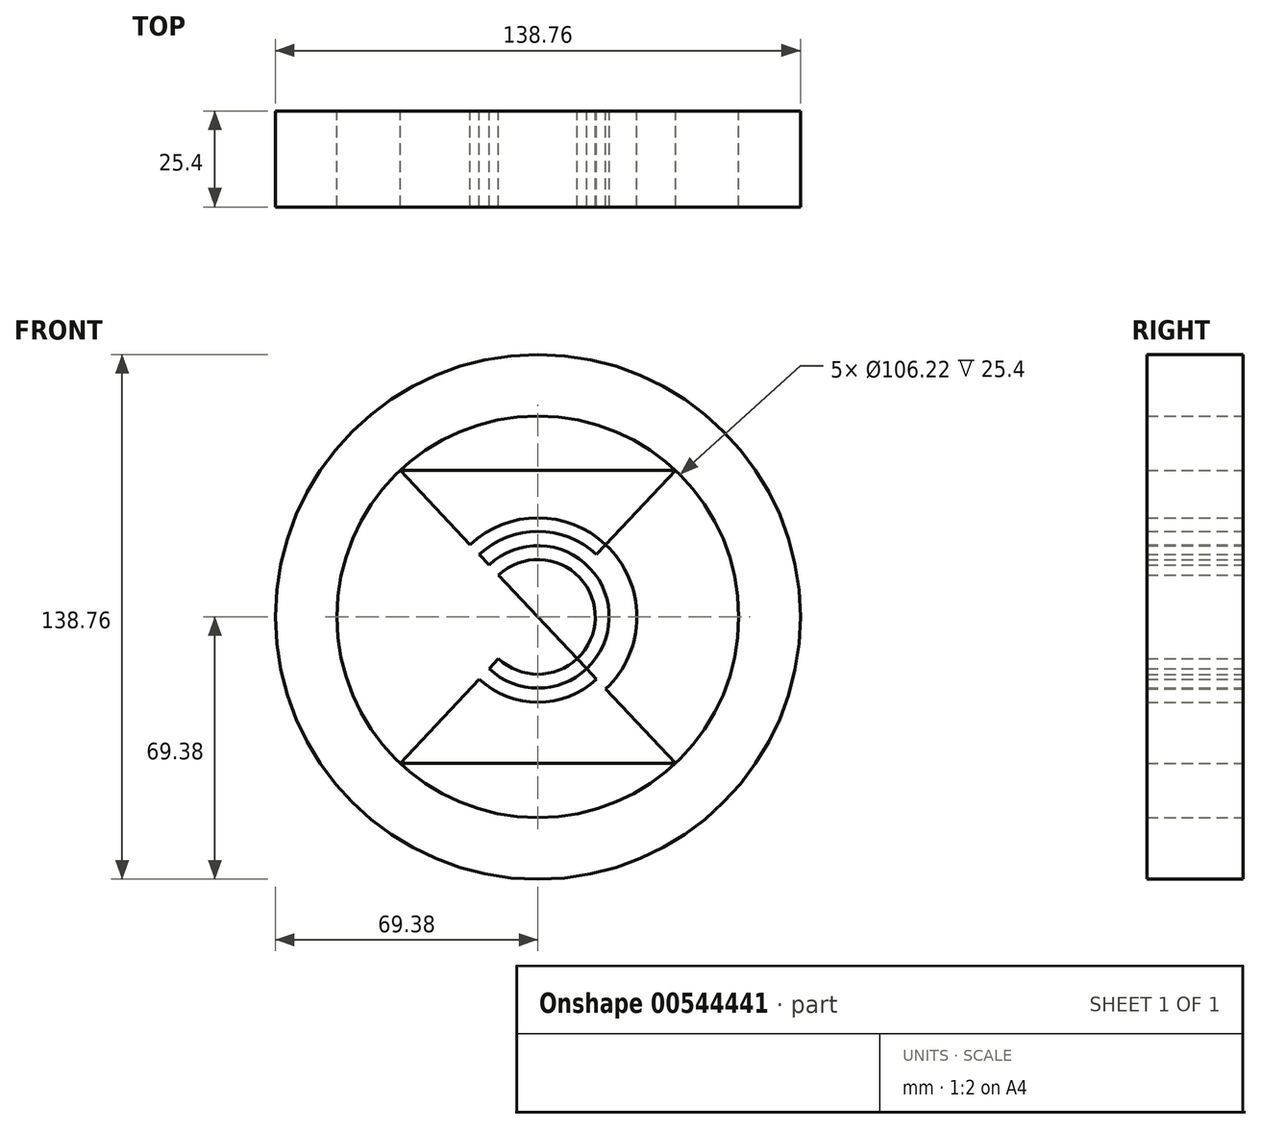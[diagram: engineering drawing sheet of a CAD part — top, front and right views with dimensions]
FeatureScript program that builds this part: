
annotation { "Feature Type Name" : "Feature", "Feature Type Description" : "" }
export const myFeature = defineFeature(function(context is Context, id is Id, definition is map)
    precondition{}
    {
        {
            var Q0;
            Q0=qCreatedBy(makeId("Front.planeOp"),FACE);
            var sketch = newSketch(context, id + "F0", { "sketchPlane" : qUnion([Q0])});
            skCircle(sketch, "E0", {"center": v(0, 0) * mm, "radius": 69.38 * mm});
            skCircle(sketch, "E1", {"center": v(0, 0) * mm, "radius": 63.29 * mm});
            skCircle(sketch, "E2", {"center": v(0, 0) * mm, "radius": 58 * mm});
            skCircle(sketch, "E3", {"center": v(0, 0) * mm, "radius": 53.11 * mm});
            skCircle(sketch, "E4", {"center": v(0, 0) * mm, "radius": 26.19 * mm});
            skCircle(sketch, "E5", {"center": v(0, 0) * mm, "radius": 22.6 * mm});
            skCircle(sketch, "E6", {"center": v(0, 0) * mm, "radius": 18.83 * mm});
            skCircle(sketch, "E7", {"center": v(0, 0) * mm, "radius": 15.17 * mm});
            skLineSegment(sketch, "E8", {"start": v(0, 0) * mm, "end": v(-36.38, 38.69) * mm});
            skLineSegment(sketch, "E9", {"start": v(-36.38, 38.69) * mm, "end": v(36.38, 38.69) * mm});
            skLineSegment(sketch, "E10", {"start": v(36.38, 38.69) * mm, "end": v(0, 0) * mm});
            skLineSegment(sketch, "E11", {"start": v(0, 0) * mm, "end": v(-36.38, -38.69) * mm});
            skLineSegment(sketch, "E12", {"start": v(-36.38, -38.69) * mm, "end": v(36.38, -38.69) * mm});
            skLineSegment(sketch, "E13", {"start": v(36.38, -38.69) * mm, "end": v(0, 0) * mm});
            skSolve(sketch);
        }
        {
            var Q0;
            Q0 = qSketchRegion(id + "F0", true);
            var Q1;
            {var subQ5=sQuery(id+"F0.wireOp",EDGE,"E12");Q1=makeQuery(id+"F0.imprint","IMPRINT",FACE,{"disambiguationData":[TD([[makeQuery(id+"F0.imprint","IMPRINT",EDGE,{"derivedFrom":subQ5}),1.0]])]});}
            var Q2;
            Q2=makeQuery(id+"F0.imprint","IMPRINT",FACE,{"disambiguationData":[TD([[makeQuery(id+"F0.imprint","IMPRINT",EDGE,{"derivedFrom":sQuery(id+"F0.wireOp",EDGE,"E2")}),1.0]])]});
            var Q3;
            {var subQ5=sQuery(id+"F0.wireOp",EDGE,"E9");Q3=makeQuery(id+"F0.imprint","IMPRINT",FACE,{"disambiguationData":[TD([[makeQuery(id+"F0.imprint","IMPRINT",EDGE,{"derivedFrom":subQ5}),-1.0]])]});}
            var Q4;
            {var subQ0=sQuery(id+"F0.wireOp",EDGE,"E8");var subQ1=sQuery(id+"F0.wireOp",EDGE,"E7");var subQ2=makeQuery(id+"F0.imprint","INTERSECT",VERTEX,{"derivedFrom":[subQ1,subQ0]});Q4=makeQuery(id+"F0.imprint","IMPRINT",FACE,{"disambiguationData":[TD([[makeQuery(id+"F0.imprint","IMPRINT",EDGE,{"disambiguationData":[TD([[subQ2,1.0]])],"derivedFrom":subQ1}),1.0]])]});}
            var Q5;
            {var subQ0=sQuery(id+"F0.wireOp",EDGE,"E11");var subQ1=sQuery(id+"F0.wireOp",EDGE,"E6");var subQ2=makeQuery(id+"F0.imprint","INTERSECT",VERTEX,{"derivedFrom":[subQ1,subQ0]});Q5=makeQuery(id+"F0.imprint","IMPRINT",FACE,{"disambiguationData":[TD([[makeQuery(id+"F0.imprint","IMPRINT",EDGE,{"disambiguationData":[TD([[subQ2,-1.0]])],"derivedFrom":subQ1}),1.0]])]});}
            var Q6;
            {var subQ0=sQuery(id+"F0.wireOp",EDGE,"E10");var subQ1=sQuery(id+"F0.wireOp",EDGE,"E5");var subQ2=makeQuery(id+"F0.imprint","INTERSECT",VERTEX,{"derivedFrom":[subQ1,subQ0]});Q6=makeQuery(id+"F0.imprint","IMPRINT",FACE,{"disambiguationData":[TD([[makeQuery(id+"F0.imprint","IMPRINT",EDGE,{"disambiguationData":[TD([[subQ2,1.0]])],"derivedFrom":subQ1}),1.0]])]});}
            var Q7;
            {var subQ0=sQuery(id+"F0.wireOp",EDGE,"E8");var subQ1=sQuery(id+"F0.wireOp",EDGE,"E5");var subQ2=makeQuery(id+"F0.imprint","INTERSECT",VERTEX,{"derivedFrom":[subQ1,subQ0]});Q7=makeQuery(id+"F0.imprint","IMPRINT",FACE,{"disambiguationData":[TD([[makeQuery(id+"F0.imprint","IMPRINT",EDGE,{"disambiguationData":[TD([[subQ2,1.0]])],"derivedFrom":subQ1}),1.0]])]});}
            var Q8;
            Q8=makeQuery(id+"F0.imprint","IMPRINT",FACE,{"disambiguationData":[TD([[makeQuery(id+"F0.imprint","IMPRINT",EDGE,{"derivedFrom":sQuery(id+"F0.wireOp",EDGE,"E1")}),1.0]])]});
            var Q9;
            {var subQ0=sQuery(id+"F0.wireOp",EDGE,"E10");var subQ1=sQuery(id+"F0.wireOp",EDGE,"E7");var subQ2=makeQuery(id+"F0.imprint","INTERSECT",VERTEX,{"derivedFrom":[subQ1,subQ0]});Q9=makeQuery(id+"F0.imprint","IMPRINT",FACE,{"disambiguationData":[TD([[makeQuery(id+"F0.imprint","IMPRINT",EDGE,{"disambiguationData":[TD([[subQ2,1.0]])],"derivedFrom":subQ1}),1.0]])]});}
            var Q10;
            {var subQ0=sQuery(id+"F0.wireOp",EDGE,"E10");var subQ1=sQuery(id+"F0.wireOp",EDGE,"E4");var subQ2=makeQuery(id+"F0.imprint","INTERSECT",VERTEX,{"derivedFrom":[subQ1,subQ0]});Q10=makeQuery(id+"F0.imprint","IMPRINT",FACE,{"disambiguationData":[TD([[makeQuery(id+"F0.imprint","IMPRINT",EDGE,{"disambiguationData":[TD([[subQ2,1.0]])],"derivedFrom":subQ1}),1.0]])]});}
            var Q11;
            {var subQ0=sQuery(id+"F0.wireOp",EDGE,"E11");var subQ1=sQuery(id+"F0.wireOp",EDGE,"E4");var subQ2=makeQuery(id+"F0.imprint","INTERSECT",VERTEX,{"derivedFrom":[subQ1,subQ0]});Q11=makeQuery(id+"F0.imprint","IMPRINT",FACE,{"disambiguationData":[TD([[makeQuery(id+"F0.imprint","IMPRINT",EDGE,{"disambiguationData":[TD([[subQ2,-1.0]])],"derivedFrom":subQ1}),1.0]])]});}
            extrude(context, id + "F1", {"entities" : qUnion([Q0, Q1, Q2, Q3, Q4, Q5, Q6, Q7, Q8, Q9, Q10, Q11]), "depth" : 25.4 * mm, "offsetDistance" : 25.4 * mm});
        }
    });
